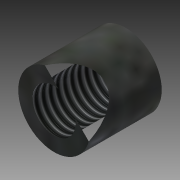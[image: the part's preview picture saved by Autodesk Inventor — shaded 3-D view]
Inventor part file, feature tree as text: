
AUTODESK INVENTOR PART (.ipt)
format: ipt  version: 2015 SP1 (Build 190203100, 203)  size: 94,720 bytes
history: native  units: mm
features: extrude x1, thread x1, sketch x1
ambient origin geometry x8: Origin, YZ Plane, XZ Plane, XY Plane, X Axis, Y Axis, Z Axis, Center Point
bodies: Solid1 (feature_tree)
feature tree (3):
  extrude  "Extrusion1"  Depth=10.0mm
  thread  "Thread1"  [1 undecoded]
  sketch  "Sketch1"  dims[d0=5.0mm d1=3.0mm d2=5.0mm d3=0.0mm d4=10.0mm d5=0.0mm]
note: 1 required parameter value undecoded (feature->parameter linkage not recoverable at this tier; creation-order binding heuristic only, values carry confidence <= 0.55)
